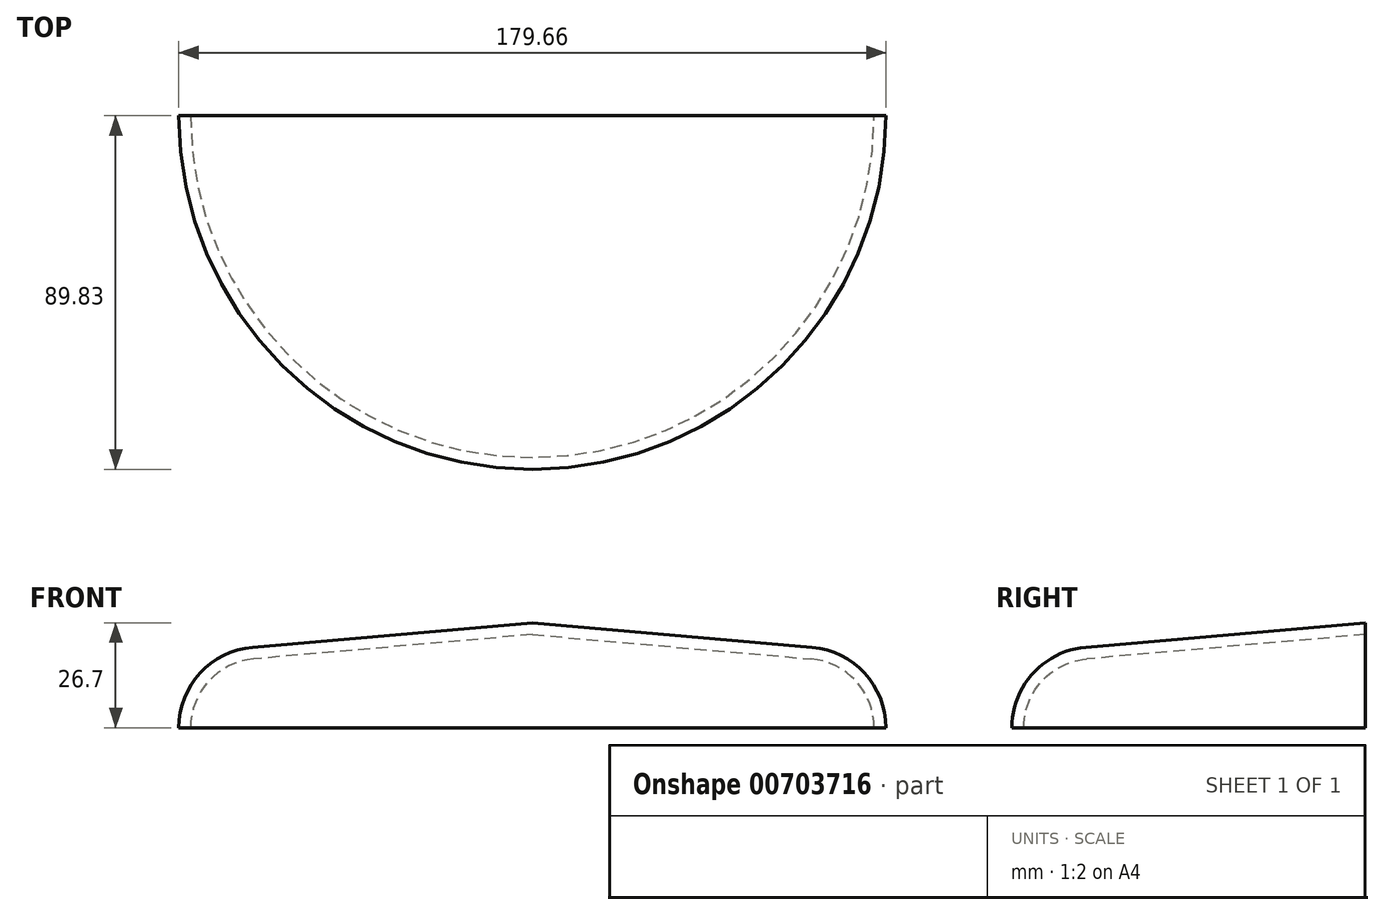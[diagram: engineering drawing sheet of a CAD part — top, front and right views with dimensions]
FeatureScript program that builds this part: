
annotation { "Feature Type Name" : "Feature", "Feature Type Description" : "" }
export const myFeature = defineFeature(function(context is Context, id is Id, definition is map)
    precondition{}
    {
        {
            var Q0;
            Q0=qCreatedBy(makeId("Right.planeOp"),FACE);
            var sketch = newSketch(context, id + "F0", { "sketchPlane" : qUnion([Q0])});
            skLineSegment(sketch, "E0", {"start": v(0, 74.02) * mm, "end": v(0, -75.03) * mm});
            skLineSegment(sketch, "E1", {"start": v(0, 50.23) * mm, "end": v(-71.06, 44.01) * mm});
            skArc(sketch, "E2", {"start": v(-71.06, 44.01) * mm, "mid": v(-84.43, 37.42) * mm, "end": v(-89.83, 23.53) * mm});
            skArc(sketch, "E3.0", {"start": v(-70.8, 41.03) * mm, "mid": v(-82.22, 35.4) * mm, "end": v(-86.83, 23.53) * mm});
            skLineSegment(sketch, "E3.1", {"start": v(0, 47.22) * mm, "end": v(-70.8, 41.03) * mm});
            skLineSegment(sketch, "E4", {"start": v(-69.27, 23.53) * mm, "end": v(-89.83, 23.53) * mm, "construction": true});
            skLineSegment(sketch, "E5", {"start": v(-89.83, 23.53) * mm, "end": v(-86.83, 23.53) * mm});
            skLineSegment(sketch, "E6", {"start": v(0, 50.23) * mm, "end": v(0, 47.22) * mm});
            skSolve(sketch);
        }
        {
            var Q0;
            Q0=makeQuery(id+"F0.imprint","IMPRINT",FACE,{"disambiguationData":[TD([[makeQuery(id+"F0.imprint","IMPRINT",EDGE,{"derivedFrom":sQuery(id+"F0.wireOp",EDGE,"E1")}),1.0]])]});
            var Q1;
            Q1=sQuery(id+"F0.wireOp",EDGE,"E0");
            revolve(context, id + "F1", {"surfaceOperationType" : NewSurfaceOperationType.NEW, "entities" : qUnion([Q0]), "axis" : qUnion([Q1]), "revolveType" : RevolveType.SYMMETRIC, "angle" : 180 * degree});
        }
    });
